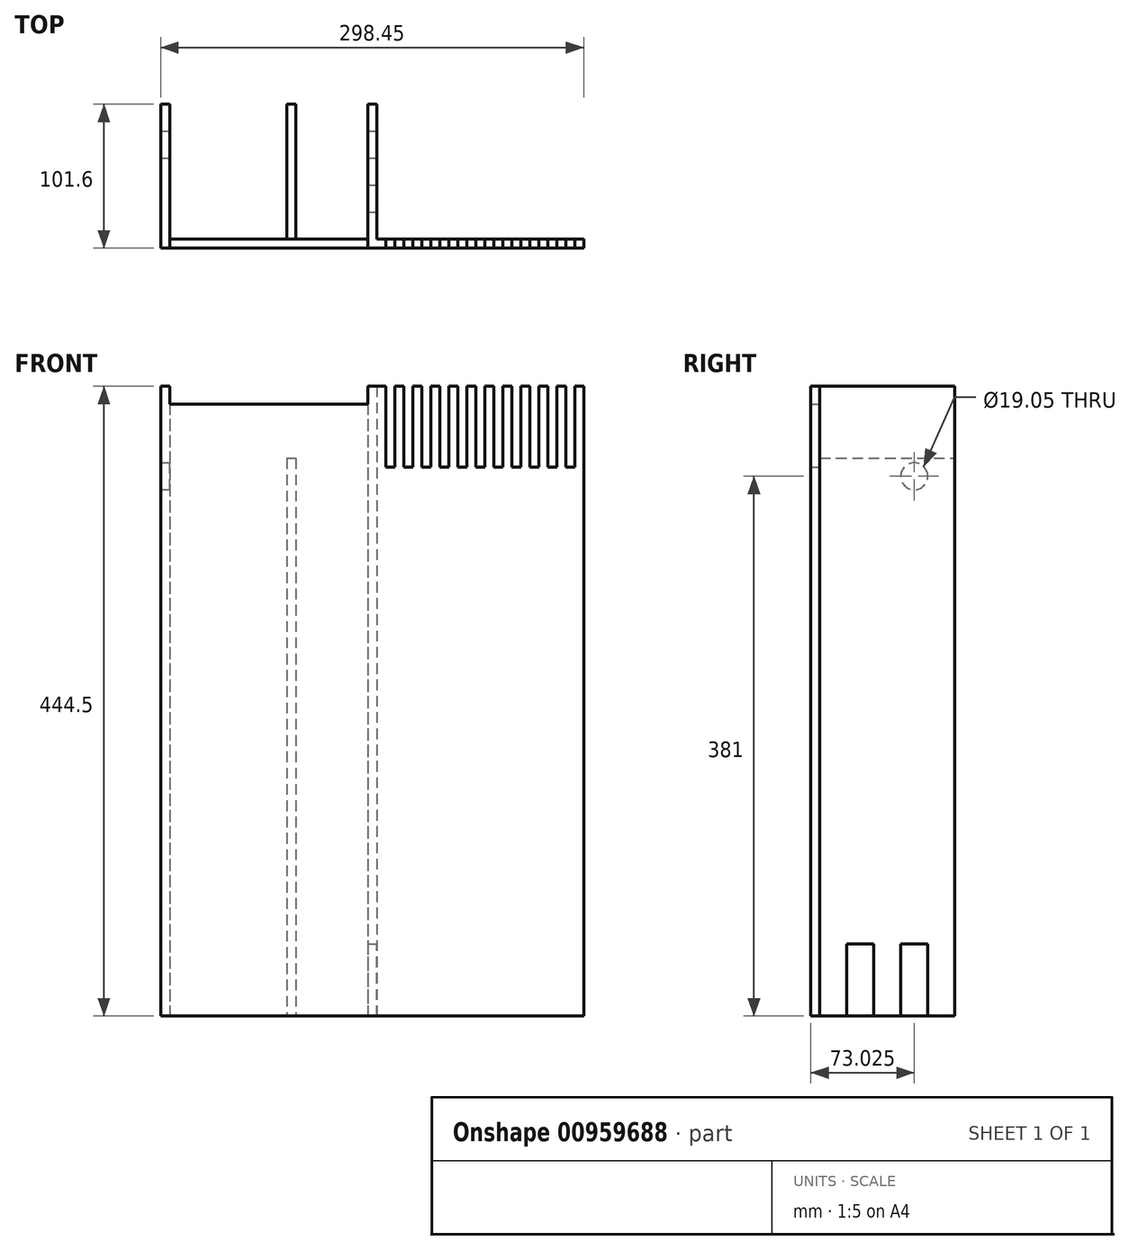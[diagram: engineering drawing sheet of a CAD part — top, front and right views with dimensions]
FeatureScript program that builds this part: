
annotation { "Feature Type Name" : "Feature", "Feature Type Description" : "" }
export const myFeature = defineFeature(function(context is Context, id is Id, definition is map)
    precondition{}
    {
        {
            var Q0;
            Q0=qCreatedBy(makeId("Front.planeOp"),FACE);
            var sketch = newSketch(context, id + "F0", { "sketchPlane" : qUnion([Q0])});
            skLineSegment(sketch, "E0.bottom", {"start": v(-806.63, 444.5) * mm, "end": v(-508.18, 444.5) * mm});
            skLineSegment(sketch, "E0.top", {"start": v(-806.63, 0) * mm, "end": v(-508.18, 0) * mm});
            skLineSegment(sketch, "E0.left", {"start": v(-806.63, 444.5) * mm, "end": v(-806.63, 0) * mm});
            skLineSegment(sketch, "E0.right", {"start": v(-508.18, 444.5) * mm, "end": v(-508.18, 0) * mm});
            skSolve(sketch);
        }
        {
            var Q0;
            Q0=makeQuery(id+"F0.imprint","IMPRINT",FACE,{"disambiguationData":[TD([[makeQuery(id+"F0.imprint","IMPRINT",EDGE,{"derivedFrom":sQuery(id+"F0.wireOp",EDGE,"E0.bottom")}),-1.0]])]});
            extrude(context, id + "F1", {"entities" : qUnion([Q0]), "depth" : 6.35 * mm, "offsetDistance" : 25.4 * mm});
        }
        {
            var Q0;
            Q0=makeQuery(id+"F1.opExtrude","CAP_FACE",FACE,{"disambiguationData":[OSD([sQuery(id+"F0.wireOp",EDGE,"E0.bottom"),sQuery(id+"F0.wireOp",EDGE,"E0.top"),sQuery(id+"F0.wireOp",EDGE,"E0.left"),sQuery(id+"F0.wireOp",EDGE,"E0.right")])],"isStart":true});
            var sketch = newSketch(context, id + "F2", { "sketchPlane" : qUnion([Q0])});
            skLineSegment(sketch, "E1.bottom", {"start": v(806.63, 444.5) * mm, "end": v(800.28, 444.5) * mm});
            skLineSegment(sketch, "E1.top", {"start": v(806.63, 0) * mm, "end": v(800.28, 0) * mm});
            skLineSegment(sketch, "E1.left", {"start": v(806.63, 444.5) * mm, "end": v(806.63, 0) * mm});
            skLineSegment(sketch, "E1.right", {"start": v(800.28, 444.5) * mm, "end": v(800.28, 0) * mm});
            skSolve(sketch);
        }
        {
            var Q0;
            Q0 = qSketchRegion(id + "F2", true);
            extrude(context, id + "F3", {"entities" : qUnion([Q0]), "operationType" : NewBodyOperationType.ADD, "depth" : 95.25 * mm, "offsetDistance" : 25.4 * mm});
        }
        {
            var Q0;
            Q0=makeQuery(id+"F1.opExtrude","CAP_FACE",FACE,{"disambiguationData":[OSD([sQuery(id+"F0.wireOp",EDGE,"E0.bottom"),sQuery(id+"F0.wireOp",EDGE,"E0.top"),sQuery(id+"F0.wireOp",EDGE,"E0.left"),sQuery(id+"F0.wireOp",EDGE,"E0.right")])],"isStart":true});
            var sketch = newSketch(context, id + "F4", { "sketchPlane" : qUnion([Q0])});
            skLineSegment(sketch, "E2.bottom", {"start": v(597.08, 444.5) * mm, "end": v(590.73, 444.5) * mm});
            skLineSegment(sketch, "E2.top", {"start": v(597.08, 387.35) * mm, "end": v(590.73, 387.35) * mm});
            skLineSegment(sketch, "E2.left", {"start": v(597.08, 444.5) * mm, "end": v(597.08, 387.35) * mm});
            skLineSegment(sketch, "E2.right", {"start": v(590.73, 444.5) * mm, "end": v(590.73, 387.35) * mm});
            skLineSegment(sketch, "E3.bottom", {"start": v(584.38, 444.5) * mm, "end": v(578.03, 444.5) * mm});
            skLineSegment(sketch, "E3.top", {"start": v(584.38, 387.35) * mm, "end": v(578.03, 387.35) * mm});
            skLineSegment(sketch, "E3.left", {"start": v(584.38, 444.5) * mm, "end": v(584.38, 387.35) * mm});
            skLineSegment(sketch, "E3.right", {"start": v(578.03, 444.5) * mm, "end": v(578.03, 387.35) * mm});
            skLineSegment(sketch, "E4.bottom", {"start": v(571.68, 444.5) * mm, "end": v(565.33, 444.5) * mm});
            skLineSegment(sketch, "E4.top", {"start": v(571.68, 387.35) * mm, "end": v(565.33, 387.35) * mm});
            skLineSegment(sketch, "E4.left", {"start": v(571.68, 444.5) * mm, "end": v(571.68, 387.35) * mm});
            skLineSegment(sketch, "E4.right", {"start": v(565.33, 444.5) * mm, "end": v(565.33, 387.35) * mm});
            skLineSegment(sketch, "E5.bottom", {"start": v(558.98, 444.5) * mm, "end": v(552.63, 444.5) * mm});
            skLineSegment(sketch, "E5.top", {"start": v(558.98, 387.35) * mm, "end": v(552.63, 387.35) * mm});
            skLineSegment(sketch, "E5.left", {"start": v(558.98, 444.5) * mm, "end": v(558.98, 387.35) * mm});
            skLineSegment(sketch, "E5.right", {"start": v(552.63, 444.5) * mm, "end": v(552.63, 387.35) * mm});
            skLineSegment(sketch, "E6.bottom", {"start": v(546.28, 444.5) * mm, "end": v(539.93, 444.5) * mm});
            skLineSegment(sketch, "E6.top", {"start": v(546.28, 387.35) * mm, "end": v(539.93, 387.35) * mm});
            skLineSegment(sketch, "E6.left", {"start": v(546.28, 444.5) * mm, "end": v(546.28, 387.35) * mm});
            skLineSegment(sketch, "E6.right", {"start": v(539.93, 444.5) * mm, "end": v(539.93, 387.35) * mm});
            skLineSegment(sketch, "E7.bottom", {"start": v(527.23, 444.5) * mm, "end": v(533.58, 444.5) * mm});
            skLineSegment(sketch, "E7.top", {"start": v(527.23, 387.35) * mm, "end": v(533.58, 387.35) * mm});
            skLineSegment(sketch, "E7.left", {"start": v(527.23, 444.5) * mm, "end": v(527.23, 387.35) * mm});
            skLineSegment(sketch, "E7.right", {"start": v(533.58, 444.5) * mm, "end": v(533.58, 387.35) * mm});
            skLineSegment(sketch, "E8.bottom", {"start": v(520.88, 444.5) * mm, "end": v(514.53, 444.5) * mm});
            skLineSegment(sketch, "E8.top", {"start": v(520.88, 387.35) * mm, "end": v(514.53, 387.35) * mm});
            skLineSegment(sketch, "E8.left", {"start": v(520.88, 444.5) * mm, "end": v(520.88, 387.35) * mm});
            skLineSegment(sketch, "E8.right", {"start": v(514.53, 444.5) * mm, "end": v(514.53, 387.35) * mm});
            skLineSegment(sketch, "E9.bottom", {"start": v(603.43, 444.5) * mm, "end": v(609.78, 444.5) * mm});
            skLineSegment(sketch, "E9.top", {"start": v(603.43, 387.35) * mm, "end": v(609.78, 387.35) * mm});
            skLineSegment(sketch, "E9.left", {"start": v(603.43, 444.5) * mm, "end": v(603.43, 387.35) * mm});
            skLineSegment(sketch, "E9.right", {"start": v(609.78, 444.5) * mm, "end": v(609.78, 387.35) * mm});
            skLineSegment(sketch, "E10.bottom", {"start": v(616.13, 444.5) * mm, "end": v(622.48, 444.5) * mm});
            skLineSegment(sketch, "E10.top", {"start": v(616.13, 387.35) * mm, "end": v(622.48, 387.35) * mm});
            skLineSegment(sketch, "E10.left", {"start": v(616.13, 444.5) * mm, "end": v(616.13, 387.35) * mm});
            skLineSegment(sketch, "E10.right", {"start": v(622.48, 444.5) * mm, "end": v(622.48, 387.35) * mm});
            skLineSegment(sketch, "E11.bottom", {"start": v(628.83, 444.5) * mm, "end": v(635.18, 444.5) * mm});
            skLineSegment(sketch, "E11.top", {"start": v(628.83, 387.35) * mm, "end": v(635.18, 387.35) * mm});
            skLineSegment(sketch, "E11.left", {"start": v(628.83, 444.5) * mm, "end": v(628.83, 387.35) * mm});
            skLineSegment(sketch, "E11.right", {"start": v(635.18, 444.5) * mm, "end": v(635.18, 387.35) * mm});
            skLineSegment(sketch, "E12.bottom", {"start": v(641.53, 444.5) * mm, "end": v(647.88, 444.5) * mm});
            skLineSegment(sketch, "E12.top", {"start": v(641.53, 387.35) * mm, "end": v(647.88, 387.35) * mm});
            skLineSegment(sketch, "E12.left", {"start": v(641.53, 444.5) * mm, "end": v(641.53, 387.35) * mm});
            skLineSegment(sketch, "E12.right", {"start": v(647.88, 444.5) * mm, "end": v(647.88, 387.35) * mm});
            skSolve(sketch);
        }
        {
            var Q0;
            Q0=makeQuery(id+"F4.imprint","IMPRINT",FACE,{"disambiguationData":[TD([[makeQuery(id+"F4.imprint","IMPRINT",EDGE,{"derivedFrom":sQuery(id+"F4.wireOp",EDGE,"E8.bottom")}),1.0]])]});
            var Q1;
            Q1=makeQuery(id+"F4.imprint","IMPRINT",FACE,{"disambiguationData":[TD([[makeQuery(id+"F4.imprint","IMPRINT",EDGE,{"derivedFrom":sQuery(id+"F4.wireOp",EDGE,"E7.bottom")}),1.0]])]});
            var Q2;
            Q2=makeQuery(id+"F4.imprint","IMPRINT",FACE,{"disambiguationData":[TD([[makeQuery(id+"F4.imprint","IMPRINT",EDGE,{"derivedFrom":sQuery(id+"F4.wireOp",EDGE,"E6.bottom")}),1.0]])]});
            var Q3;
            Q3=makeQuery(id+"F4.imprint","IMPRINT",FACE,{"disambiguationData":[TD([[makeQuery(id+"F4.imprint","IMPRINT",EDGE,{"derivedFrom":sQuery(id+"F4.wireOp",EDGE,"E5.bottom")}),1.0]])]});
            var Q4;
            Q4=makeQuery(id+"F4.imprint","IMPRINT",FACE,{"disambiguationData":[TD([[makeQuery(id+"F4.imprint","IMPRINT",EDGE,{"derivedFrom":sQuery(id+"F4.wireOp",EDGE,"E4.bottom")}),1.0]])]});
            var Q5;
            Q5=makeQuery(id+"F4.imprint","IMPRINT",FACE,{"disambiguationData":[TD([[makeQuery(id+"F4.imprint","IMPRINT",EDGE,{"derivedFrom":sQuery(id+"F4.wireOp",EDGE,"E3.bottom")}),1.0]])]});
            var Q6;
            Q6=makeQuery(id+"F4.imprint","IMPRINT",FACE,{"disambiguationData":[TD([[makeQuery(id+"F4.imprint","IMPRINT",EDGE,{"derivedFrom":sQuery(id+"F4.wireOp",EDGE,"E2.bottom")}),1.0]])]});
            var Q7;
            Q7=makeQuery(id+"F4.imprint","IMPRINT",FACE,{"disambiguationData":[TD([[makeQuery(id+"F4.imprint","IMPRINT",EDGE,{"derivedFrom":sQuery(id+"F4.wireOp",EDGE,"E9.bottom")}),1.0]])]});
            var Q8;
            Q8=makeQuery(id+"F4.imprint","IMPRINT",FACE,{"disambiguationData":[TD([[makeQuery(id+"F4.imprint","IMPRINT",EDGE,{"derivedFrom":sQuery(id+"F4.wireOp",EDGE,"E10.bottom")}),1.0]])]});
            var Q9;
            Q9=makeQuery(id+"F4.imprint","IMPRINT",FACE,{"disambiguationData":[TD([[makeQuery(id+"F4.imprint","IMPRINT",EDGE,{"derivedFrom":sQuery(id+"F4.wireOp",EDGE,"E11.bottom")}),1.0]])]});
            var Q10;
            Q10=makeQuery(id+"F4.imprint","IMPRINT",FACE,{"disambiguationData":[TD([[makeQuery(id+"F4.imprint","IMPRINT",EDGE,{"derivedFrom":sQuery(id+"F4.wireOp",EDGE,"E12.bottom")}),1.0]])]});
            extrude(context, id + "F5", {"entities" : qUnion([Q0, Q1, Q2, Q3, Q4, Q5, Q6, Q7, Q8, Q9, Q10]), "operationType" : NewBodyOperationType.REMOVE, "endBound" : BoundingType.THROUGH_ALL, "oppositeDirection" : true, "depth" : 25.4 * mm, "offsetDistance" : 25.4 * mm});
        }
        {
            var Q0;
            Q0=makeQuery(id+"F1.opExtrude","CAP_FACE",FACE,{"disambiguationData":[OSD([sQuery(id+"F0.wireOp",EDGE,"E0.bottom"),sQuery(id+"F0.wireOp",EDGE,"E0.top"),sQuery(id+"F0.wireOp",EDGE,"E0.left"),sQuery(id+"F0.wireOp",EDGE,"E0.right")])],"isStart":true});
            var sketch = newSketch(context, id + "F6", { "sketchPlane" : qUnion([Q0])});
            skLineSegment(sketch, "E13.bottom", {"start": v(660.58, 444.5) * mm, "end": v(654.23, 444.5) * mm});
            skLineSegment(sketch, "E13.top", {"start": v(660.58, 0) * mm, "end": v(654.23, 0) * mm});
            skLineSegment(sketch, "E13.left", {"start": v(660.58, 444.5) * mm, "end": v(660.58, 0) * mm});
            skLineSegment(sketch, "E13.right", {"start": v(654.23, 444.5) * mm, "end": v(654.23, 0) * mm});
            skLineSegment(sketch, "E14.bottom", {"start": v(711.38, 444.5) * mm, "end": v(717.73, 444.5) * mm});
            skLineSegment(sketch, "E14.top", {"start": v(711.38, 0) * mm, "end": v(717.73, 0) * mm});
            skLineSegment(sketch, "E14.left", {"start": v(711.38, 444.5) * mm, "end": v(711.38, 0) * mm});
            skLineSegment(sketch, "E14.right", {"start": v(717.73, 444.5) * mm, "end": v(717.73, 0) * mm});
            skSolve(sketch);
        }
        {
            var Q0;
            Q0=makeQuery(id+"F6.imprint","IMPRINT",FACE,{"disambiguationData":[TD([[makeQuery(id+"F6.imprint","IMPRINT",EDGE,{"derivedFrom":sQuery(id+"F6.wireOp",EDGE,"E13.bottom")}),1.0]])]});
            var Q1;
            Q1=makeQuery(id+"F6.imprint","IMPRINT",FACE,{"disambiguationData":[TD([[makeQuery(id+"F6.imprint","IMPRINT",EDGE,{"derivedFrom":sQuery(id+"F6.wireOp",EDGE,"E14.bottom")}),1.0]])]});
            extrude(context, id + "F7", {"entities" : qUnion([Q0, Q1]), "operationType" : NewBodyOperationType.ADD, "depth" : 95.25 * mm, "offsetDistance" : 25.4 * mm});
        }
        {
            var Q0;
            Q0=makeQuery(id+"F7.opExtrude","SWEPT_FACE",FACE,{"disambiguationData":[OSD([sQuery(id+"F6.wireOp",EDGE,"E13.right")])]});
            var sketch = newSketch(context, id + "F8", { "sketchPlane" : qUnion([Q0])});
            skLineSegment(sketch, "E15.bottom", {"start": v(19.05, 0) * mm, "end": v(38.1, 0) * mm});
            skLineSegment(sketch, "E15.top", {"start": v(19.05, 50.8) * mm, "end": v(38.1, 50.8) * mm});
            skLineSegment(sketch, "E15.left", {"start": v(19.05, 0) * mm, "end": v(19.05, 50.8) * mm});
            skLineSegment(sketch, "E15.right", {"start": v(38.1, 0) * mm, "end": v(38.1, 50.8) * mm});
            skLineSegment(sketch, "E16.bottom", {"start": v(57.15, 0) * mm, "end": v(76.2, 0) * mm});
            skLineSegment(sketch, "E16.top", {"start": v(57.15, 50.8) * mm, "end": v(76.2, 50.8) * mm});
            skLineSegment(sketch, "E16.left", {"start": v(57.15, 0) * mm, "end": v(57.15, 50.8) * mm});
            skLineSegment(sketch, "E16.right", {"start": v(76.2, 0) * mm, "end": v(76.2, 50.8) * mm});
            skSolve(sketch);
        }
        {
            var Q0;
            Q0=makeQuery(id+"F7.opExtrude","SWEPT_FACE",FACE,{"disambiguationData":[OSD([sQuery(id+"F6.wireOp",EDGE,"E14.left")])]});
            var sketch = newSketch(context, id + "F9", { "sketchPlane" : qUnion([Q0])});
            skLineSegment(sketch, "E17.bottom", {"start": v(0, 444.5) * mm, "end": v(95.25, 444.5) * mm});
            skLineSegment(sketch, "E17.top", {"start": v(0, 393.7) * mm, "end": v(95.25, 393.7) * mm});
            skLineSegment(sketch, "E17.left", {"start": v(0, 444.5) * mm, "end": v(0, 393.7) * mm});
            skLineSegment(sketch, "E17.right", {"start": v(95.25, 444.5) * mm, "end": v(95.25, 393.7) * mm});
            skSolve(sketch);
        }
        {
            var Q0;
            Q0=makeQuery(id+"F8.imprint","IMPRINT",FACE,{"disambiguationData":[TD([[makeQuery(id+"F8.imprint","IMPRINT",EDGE,{"derivedFrom":sQuery(id+"F8.wireOp",EDGE,"E15.bottom")}),-1.0]])]});
            var Q1;
            Q1=makeQuery(id+"F8.imprint","IMPRINT",FACE,{"disambiguationData":[TD([[makeQuery(id+"F8.imprint","IMPRINT",EDGE,{"derivedFrom":sQuery(id+"F8.wireOp",EDGE,"E16.bottom")}),-1.0]])]});
            var Q2;
            Q2=makeQuery(id+"F9.imprint","IMPRINT",FACE,{"disambiguationData":[TD([[makeQuery(id+"F9.imprint","IMPRINT",EDGE,{"derivedFrom":sQuery(id+"F9.wireOp",EDGE,"E17.bottom")}),1.0]])]});
            extrude(context, id + "F10", {"entities" : qUnion([Q0, Q1, Q2]), "operationType" : NewBodyOperationType.REMOVE, "oppositeDirection" : true, "depth" : 25.4 * mm, "offsetDistance" : 25.4 * mm});
        }
        {
            var Q0;
            {var subQ2=sQuery(id+"F0.wireOp",EDGE,"E0.top");var subQ5=sQuery(id+"F0.wireOp",EDGE,"E0.bottom");var subQ10=makeQuery(id+"F1.opExtrude","CAP_FACE",FACE,{"disambiguationData":[OSD([subQ5,subQ2,sQuery(id+"F0.wireOp",EDGE,"E0.left"),sQuery(id+"F0.wireOp",EDGE,"E0.right")])],"isStart":true});Q0=makeQuery(id+"F10.boolean.opBoolean","MERGE",FACE,{"derivedFrom":[makeQuery(id+"F7.boolean.opBoolean","SPLIT",FACE,{"disambiguationData":[TD([makeQuery(id+"F3.opExtrude","SWEPT_FACE",FACE,{"disambiguationData":[OSD([sQuery(id+"F2.wireOp",EDGE,"E1.right")])]})])],"derivedFrom":subQ10}),makeQuery(id+"F7.boolean.opBoolean","SPLIT",FACE,{"disambiguationData":[TD([makeQuery(id+"F7.opExtrude","SWEPT_FACE",FACE,{"disambiguationData":[OSD([sQuery(id+"F6.wireOp",EDGE,"E13.left")])]})])],"derivedFrom":subQ10})],"fromTools":[makeQuery(id+"F10.opExtrude","SWEPT_FACE",FACE,{"disambiguationData":[OSD([sQuery(id+"F9.wireOp",EDGE,"E17.left")])]})]});}
            var sketch = newSketch(context, id + "F11", { "sketchPlane" : qUnion([Q0])});
            skLineSegment(sketch, "E18.bottom", {"start": v(660.58, 444.5) * mm, "end": v(800.28, 444.5) * mm});
            skLineSegment(sketch, "E18.top", {"start": v(660.58, 431.8) * mm, "end": v(800.28, 431.8) * mm});
            skLineSegment(sketch, "E18.left", {"start": v(660.58, 444.5) * mm, "end": v(660.58, 431.8) * mm});
            skLineSegment(sketch, "E18.right", {"start": v(800.28, 444.5) * mm, "end": v(800.28, 431.8) * mm});
            skSolve(sketch);
        }
        {
            var Q0;
            Q0=makeQuery(id+"F11.imprint","IMPRINT",FACE,{"disambiguationData":[TD([[makeQuery(id+"F11.imprint","IMPRINT",EDGE,{"derivedFrom":sQuery(id+"F11.wireOp",EDGE,"E18.bottom")}),1.0]])]});
            extrude(context, id + "F12", {"entities" : qUnion([Q0]), "operationType" : NewBodyOperationType.REMOVE, "oppositeDirection" : true, "depth" : 25.4 * mm, "offsetDistance" : 25.4 * mm});
        }
        {
            var Q0;
            Q0=makeQuery(id+"F12.boolean.opBoolean","MERGE",FACE,{"derivedFrom":[makeQuery(id+"F3.opExtrude","SWEPT_FACE",FACE,{"disambiguationData":[OSD([sQuery(id+"F2.wireOp",EDGE,"E1.right")])]})],"fromTools":[makeQuery(id+"F12.opExtrude","SWEPT_FACE",FACE,{"disambiguationData":[OSD([sQuery(id+"F11.wireOp",EDGE,"E18.right")])]})]});
            var sketch = newSketch(context, id + "F13", { "sketchPlane" : qUnion([Q0])});
            skCircle(sketch, "E19", {"center": v(66.68, 381) * mm, "radius": 9.53 * mm});
            skSolve(sketch);
        }
        {
            var Q0;
            Q0=makeQuery(id+"F13.imprint","IMPRINT",FACE,{"disambiguationData":[TD([[makeQuery(id+"F13.imprint","IMPRINT",EDGE,{"derivedFrom":sQuery(id+"F13.wireOp",EDGE,"E19")}),1.0]])]});
            extrude(context, id + "F14", {"entities" : qUnion([Q0]), "operationType" : NewBodyOperationType.REMOVE, "oppositeDirection" : true, "depth" : 25.4 * mm, "offsetDistance" : 25.4 * mm});
        }
    });
